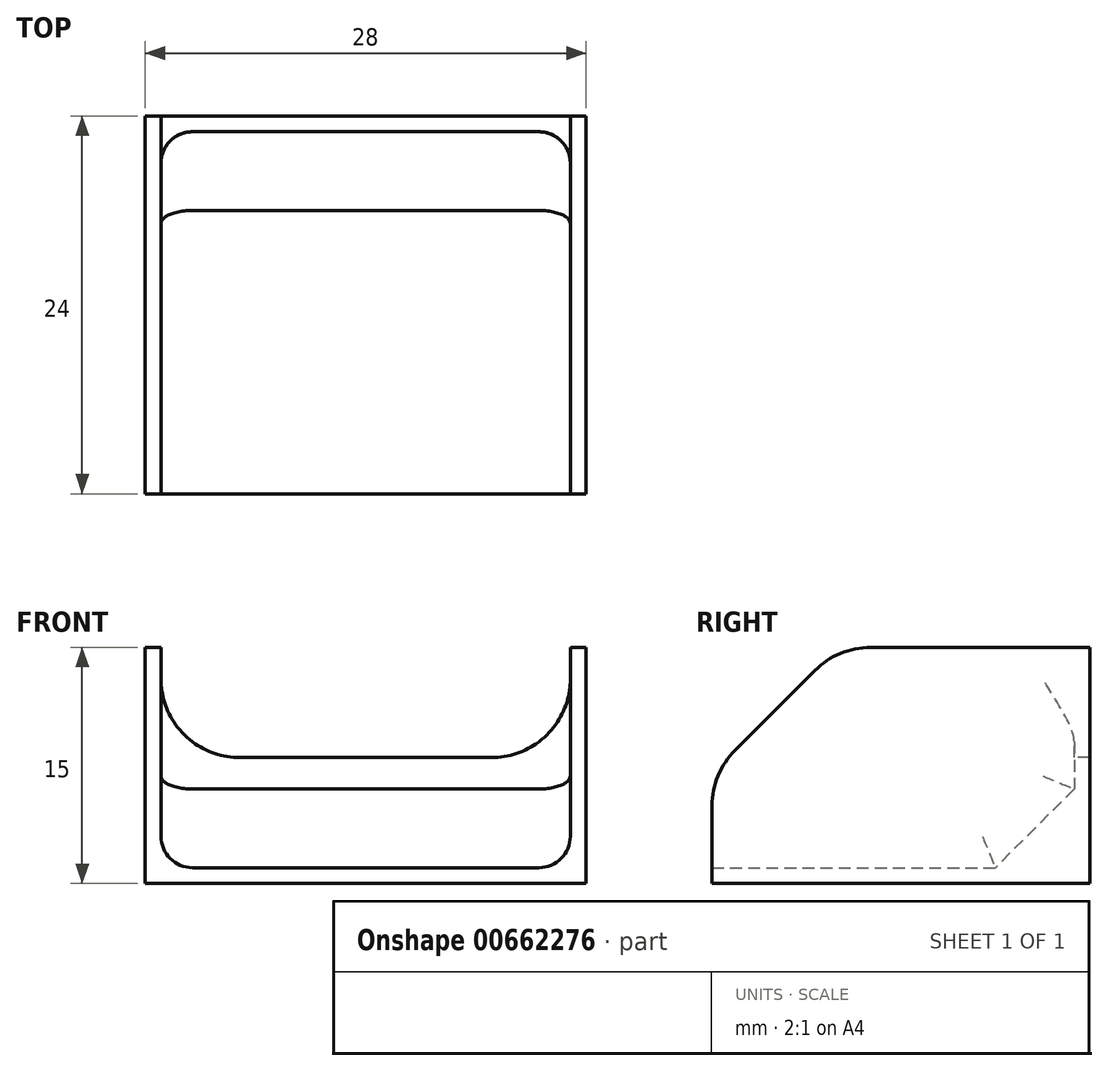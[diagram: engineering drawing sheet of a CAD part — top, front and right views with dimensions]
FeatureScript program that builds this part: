
annotation { "Feature Type Name" : "Feature", "Feature Type Description" : "" }
export const myFeature = defineFeature(function(context is Context, id is Id, definition is map)
    precondition{}
    {
        {
            var Q0;
            Q0=qCreatedBy(makeId("Top.planeOp"),FACE);
            var sketch = newSketch(context, id + "F0", { "sketchPlane" : qUnion([Q0])});
            skLineSegment(sketch, "E0.bottom", {"start": v(-34.7, 0) * mm, "end": v(-62.7, 0) * mm});
            skLineSegment(sketch, "E0.top", {"start": v(-34.7, 24) * mm, "end": v(-62.7, 24) * mm});
            skLineSegment(sketch, "E0.left", {"start": v(-34.7, 0) * mm, "end": v(-34.7, 24) * mm});
            skLineSegment(sketch, "E0.right", {"start": v(-62.7, 0) * mm, "end": v(-62.7, 24) * mm});
            skSolve(sketch);
        }
        {
            var Q0;
            Q0=makeQuery(id+"F0.imprint","IMPRINT",FACE,{"disambiguationData":[TD([[makeQuery(id+"F0.imprint","IMPRINT",EDGE,{"derivedFrom":sQuery(id+"F0.wireOp",EDGE,"E0.bottom")}),-1.0]])]});
            var sketch = newSketch(context, id + "F1", { "sketchPlane" : qUnion([Q0])});
            skSolve(sketch);
        }
        {
            var Q0;
            Q0=makeQuery(id+"F1.imprint","IMPRINT",FACE,{"disambiguationData":[TD([[makeQuery(id+"F1.imprint","IMPRINT",EDGE,{"derivedFrom":makeQuery(id+"F0.imprint","IMPRINT",EDGE,{"derivedFrom":sQuery(id+"F0.wireOp",EDGE,"E0.bottom")})}),-1.0]])]});
            extrude(context, id + "F2", {"entities" : qUnion([Q0]), "depth" : 15 * mm, "offsetDistance" : 25 * mm});
        }
        {
            var Q0;
            Q0=makeQuery(id+"F2.opExtrude","CAP_FACE",FACE,{"disambiguationData":[OSD([sQuery(id+"F0.wireOp",EDGE,"E0.bottom"),sQuery(id+"F0.wireOp",EDGE,"E0.top"),sQuery(id+"F0.wireOp",EDGE,"E0.left"),sQuery(id+"F0.wireOp",EDGE,"E0.right")])],"isStart":false});
            shell(context, id + "F3", {"entities" : qUnion([Q0]), "thickness" : 1 * mm});
        }
        {
            var Q0;
            Q0=makeQuery(id+"F3.opShell","OFFSET_FACE",FACE,{"disambiguationData":[OSD([sQuery(id+"F0.wireOp",EDGE,"E0.bottom")])]});
            extrude(context, id + "F4", {"entities" : qUnion([Q0]), "operationType" : NewBodyOperationType.REMOVE, "oppositeDirection" : true, "depth" : 25 * mm, "offsetDistance" : 25 * mm});
        }
        {
            var Q0;
            {var subQ0=sQuery(id+"F0.wireOp",EDGE,"E0.right");var subQ1=sQuery(id+"F0.wireOp",EDGE,"E0.bottom");Q0=makeQuery(id+"F4.boolean.opBoolean","SPLIT",EDGE,{"disambiguationData":[TD([makeQuery(id+"F2.opExtrude","SWEPT_FACE",FACE,{"disambiguationData":[OSD([subQ0])]})])],"derivedFrom":makeQuery(id+"F2.opExtrude","CAP_EDGE",EDGE,{"disambiguationData":[OSD([subQ1])],"isStart":false})});}
            var Q1;
            {var subQ0=sQuery(id+"F0.wireOp",EDGE,"E0.left");var subQ1=sQuery(id+"F0.wireOp",EDGE,"E0.bottom");Q1=makeQuery(id+"F4.boolean.opBoolean","SPLIT",EDGE,{"disambiguationData":[TD([makeQuery(id+"F2.opExtrude","SWEPT_FACE",FACE,{"disambiguationData":[OSD([subQ0])]})])],"derivedFrom":makeQuery(id+"F2.opExtrude","CAP_EDGE",EDGE,{"disambiguationData":[OSD([subQ1])],"isStart":false})});}
            chamfer(context, id + "F5", {"entities" : qUnion([Q0, Q1]), "width" : 8 * mm, "tangentPropagation" : true});
        }
        {
            var Q0;
            {var subQ0=sQuery(id+"F0.wireOp",EDGE,"E0.bottom");var subQ1=makeQuery(id+"F2.opExtrude","SWEPT_FACE",FACE,{"disambiguationData":[OSD([subQ0])]});var subQ2=sQuery(id+"F0.wireOp",EDGE,"E0.right");Q0=makeQuery(id+"F5.opChamfer","BLEND_EDGE",EDGE,{"blendedFrom":[makeQuery(id+"F4.boolean.opBoolean","SPLIT",EDGE,{"disambiguationData":[TD([makeQuery(id+"F2.opExtrude","SWEPT_FACE",FACE,{"disambiguationData":[OSD([subQ2])]})])],"derivedFrom":makeQuery(id+"F2.opExtrude","CAP_EDGE",EDGE,{"disambiguationData":[OSD([subQ0])],"isStart":false})}),subQ1],"blendedInto":[subQ1]});}
            var Q1;
            {var subQ0=sQuery(id+"F0.wireOp",EDGE,"E0.right");var subQ1=sQuery(id+"F0.wireOp",EDGE,"E0.bottom");var subQ2=makeQuery(id+"F2.opExtrude","CAP_FACE",FACE,{"disambiguationData":[OSD([subQ1,sQuery(id+"F0.wireOp",EDGE,"E0.top"),sQuery(id+"F0.wireOp",EDGE,"E0.left"),subQ0])],"isStart":false});Q1=makeQuery(id+"F5.opChamfer","BLEND_EDGE",EDGE,{"blendedFrom":[makeQuery(id+"F4.boolean.opBoolean","SPLIT",EDGE,{"disambiguationData":[TD([makeQuery(id+"F2.opExtrude","SWEPT_FACE",FACE,{"disambiguationData":[OSD([subQ0])]})])],"derivedFrom":makeQuery(id+"F2.opExtrude","CAP_EDGE",EDGE,{"disambiguationData":[OSD([subQ1])],"isStart":false})}),subQ2],"blendedInto":[subQ2]});}
            var Q2;
            {var subQ0=sQuery(id+"F0.wireOp",EDGE,"E0.left");var subQ1=sQuery(id+"F0.wireOp",EDGE,"E0.bottom");var subQ2=makeQuery(id+"F2.opExtrude","CAP_FACE",FACE,{"disambiguationData":[OSD([subQ1,sQuery(id+"F0.wireOp",EDGE,"E0.top"),subQ0,sQuery(id+"F0.wireOp",EDGE,"E0.right")])],"isStart":false});Q2=makeQuery(id+"F5.opChamfer","BLEND_EDGE",EDGE,{"blendedFrom":[makeQuery(id+"F4.boolean.opBoolean","SPLIT",EDGE,{"disambiguationData":[TD([makeQuery(id+"F2.opExtrude","SWEPT_FACE",FACE,{"disambiguationData":[OSD([subQ0])]})])],"derivedFrom":makeQuery(id+"F2.opExtrude","CAP_EDGE",EDGE,{"disambiguationData":[OSD([subQ1])],"isStart":false})}),subQ2],"blendedInto":[subQ2]});}
            var Q3;
            {var subQ0=sQuery(id+"F0.wireOp",EDGE,"E0.bottom");var subQ1=makeQuery(id+"F2.opExtrude","SWEPT_FACE",FACE,{"disambiguationData":[OSD([subQ0])]});var subQ2=sQuery(id+"F0.wireOp",EDGE,"E0.left");Q3=makeQuery(id+"F5.opChamfer","BLEND_EDGE",EDGE,{"blendedFrom":[makeQuery(id+"F4.boolean.opBoolean","SPLIT",EDGE,{"disambiguationData":[TD([makeQuery(id+"F2.opExtrude","SWEPT_FACE",FACE,{"disambiguationData":[OSD([subQ2])]})])],"derivedFrom":makeQuery(id+"F2.opExtrude","CAP_EDGE",EDGE,{"disambiguationData":[OSD([subQ0])],"isStart":false})}),subQ1],"blendedInto":[subQ1]});}
            fillet(context, id + "F6", {"entities" : qUnion([Q0, Q1, Q2, Q3]), "radius" : 5 * mm, "tangentPropagation" : true, "allowEdgeOverflow" : false});
        }
        {
            var Q0;
            Q0=makeQuery(id+"F3.opShell","OFFSET_FACE",FACE,{"disambiguationData":[OSD([sQuery(id+"F0.wireOp",EDGE,"E0.top")])]});
            var sketch = newSketch(context, id + "F7", { "sketchPlane" : qUnion([Q0])});
            skLineSegment(sketch, "E1.bottom", {"start": v(-61.7, 15) * mm, "end": v(-35.7, 15) * mm});
            skLineSegment(sketch, "E1.top", {"start": v(-61.7, 8) * mm, "end": v(-35.7, 8) * mm});
            skLineSegment(sketch, "E1.left", {"start": v(-61.7, 15) * mm, "end": v(-61.7, 8) * mm});
            skLineSegment(sketch, "E1.right", {"start": v(-35.7, 15) * mm, "end": v(-35.7, 8) * mm});
            skSolve(sketch);
        }
        {
            var Q0;
            Q0 = qSketchRegion(id + "F7", true);
            extrude(context, id + "F8", {"entities" : qUnion([Q0]), "operationType" : NewBodyOperationType.REMOVE, "oppositeDirection" : true, "depth" : 25 * mm, "offsetDistance" : 25 * mm});
        }
        {
            var Q0;
            Q0=makeQuery(id+"F8.boolean.opBoolean","COPY",EDGE,{"derivedFrom":makeQuery(id+"F8.opExtrude","SWEPT_EDGE",EDGE,{"disambiguationData":[OSD([sQuery(id+"F0.wireOp",EDGE,"E0.top"),sQuery(id+"F0.wireOp",EDGE,"E0.right"),sQuery(id+"F7.wireOp",EDGE,"E1.top"),sQuery(id+"F7.wireOp",EDGE,"E1.left")])]})});
            var Q1;
            Q1=makeQuery(id+"F8.boolean.opBoolean","COPY",EDGE,{"derivedFrom":makeQuery(id+"F8.opExtrude","SWEPT_EDGE",EDGE,{"disambiguationData":[OSD([sQuery(id+"F0.wireOp",EDGE,"E0.top"),sQuery(id+"F0.wireOp",EDGE,"E0.left"),sQuery(id+"F7.wireOp",EDGE,"E1.top"),sQuery(id+"F7.wireOp",EDGE,"E1.right")])]})});
            fillet(context, id + "F9", {"entities" : qUnion([Q0, Q1]), "radius" : 5 * mm, "tangentPropagation" : true, "allowEdgeOverflow" : false});
        }
        {
            var Q0;
            {var subQ0=sQuery(id+"F0.wireOp",EDGE,"E0.top");Q0=makeQuery(id+"F3.opShell","OFFSET_EDGE",EDGE,{"disambiguationData":[OSD([subQ0]),TDD([makeQuery(id+"F2.opExtrude","CAP_EDGE",EDGE,{"disambiguationData":[OSD([subQ0])],"isStart":true})])]});}
            chamfer(context, id + "F10", {"entities" : qUnion([Q0]), "width" : 5 * mm, "tangentPropagation" : true});
        }
        {
            var Q0;
            {var subQ0=sQuery(id+"F0.wireOp",EDGE,"E0.right");var subQ1=sQuery(id+"F0.wireOp",EDGE,"E0.bottom");Q0=makeQuery(id+"F4.boolean.opBoolean","MERGE",EDGE,{"derivedFrom":[makeQuery(id+"F3.opShell","OFFSET_EDGE",EDGE,{"disambiguationData":[OSD([subQ0]),TDD([makeQuery(id+"F2.opExtrude","CAP_EDGE",EDGE,{"disambiguationData":[OSD([subQ0])],"isStart":true})])]}),makeQuery(id+"F4.opExtrude","SWEPT_EDGE",EDGE,{"disambiguationData":[OSD([subQ1,subQ0]),TDD([makeQuery(id+"F3.opShell","OFFSET_VERTEX",VERTEX,{"disambiguationData":[OSD([subQ1,subQ0]),TDD([makeQuery(id+"F2.opExtrude","CAP_VERTEX",VERTEX,{"disambiguationData":[OSD([subQ1,subQ0])],"isStart":true})])]})])]})]});}
            var Q1;
            Q1=makeQuery(id+"F3.opShell","OFFSET_EDGE",EDGE,{"disambiguationData":[OSD([sQuery(id+"F0.wireOp",EDGE,"E0.top"),sQuery(id+"F0.wireOp",EDGE,"E0.right")])]});
            var Q2;
            {var subQ0=sQuery(id+"F0.wireOp",EDGE,"E0.right");var subQ1=sQuery(id+"F0.wireOp",EDGE,"E0.top");Q2=makeQuery(id+"F10.opChamfer","BLEND_EDGE",EDGE,{"blendedFrom":[makeQuery(id+"F3.opShell","OFFSET_EDGE",EDGE,{"disambiguationData":[OSD([subQ1]),TDD([makeQuery(id+"F2.opExtrude","CAP_EDGE",EDGE,{"disambiguationData":[OSD([subQ1])],"isStart":true})])]}),makeQuery(id+"F8.boolean.opBoolean","MERGE",FACE,{"derivedFrom":[makeQuery(id+"F4.boolean.opBoolean","MERGE",FACE,{"derivedFrom":[makeQuery(id+"F3.opShell","OFFSET_FACE",FACE,{"disambiguationData":[OSD([subQ0])]}),makeQuery(id+"F4.opExtrude","SWEPT_FACE",FACE,{"disambiguationData":[OSD([sQuery(id+"F0.wireOp",EDGE,"E0.bottom"),subQ0])]})]}),makeQuery(id+"F8.opExtrude","SWEPT_FACE",FACE,{"disambiguationData":[OSD([sQuery(id+"F7.wireOp",EDGE,"E1.left")])]})]})],"blendedInto":[makeQuery(id+"F8.boolean.opBoolean","MERGE",FACE,{"derivedFrom":[makeQuery(id+"F4.boolean.opBoolean","MERGE",FACE,{"derivedFrom":[makeQuery(id+"F3.opShell","OFFSET_FACE",FACE,{"disambiguationData":[OSD([subQ0])]}),makeQuery(id+"F4.opExtrude","SWEPT_FACE",FACE,{"disambiguationData":[OSD([sQuery(id+"F0.wireOp",EDGE,"E0.bottom"),subQ0])]})]}),makeQuery(id+"F8.opExtrude","SWEPT_FACE",FACE,{"disambiguationData":[OSD([sQuery(id+"F7.wireOp",EDGE,"E1.left")])]})]})]});}
            var Q3;
            {var subQ0=sQuery(id+"F0.wireOp",EDGE,"E0.left");var subQ1=sQuery(id+"F0.wireOp",EDGE,"E0.bottom");Q3=makeQuery(id+"F4.boolean.opBoolean","MERGE",EDGE,{"derivedFrom":[makeQuery(id+"F3.opShell","OFFSET_EDGE",EDGE,{"disambiguationData":[OSD([subQ0]),TDD([makeQuery(id+"F2.opExtrude","CAP_EDGE",EDGE,{"disambiguationData":[OSD([subQ0])],"isStart":true})])]}),makeQuery(id+"F4.opExtrude","SWEPT_EDGE",EDGE,{"disambiguationData":[OSD([subQ1,subQ0]),TDD([makeQuery(id+"F3.opShell","OFFSET_VERTEX",VERTEX,{"disambiguationData":[OSD([subQ1,subQ0]),TDD([makeQuery(id+"F2.opExtrude","CAP_VERTEX",VERTEX,{"disambiguationData":[OSD([subQ1,subQ0])],"isStart":true})])]})])]})]});}
            var Q4;
            {var subQ0=sQuery(id+"F0.wireOp",EDGE,"E0.left");var subQ1=sQuery(id+"F0.wireOp",EDGE,"E0.top");Q4=makeQuery(id+"F10.opChamfer","BLEND_EDGE",EDGE,{"blendedFrom":[makeQuery(id+"F3.opShell","OFFSET_EDGE",EDGE,{"disambiguationData":[OSD([subQ1]),TDD([makeQuery(id+"F2.opExtrude","CAP_EDGE",EDGE,{"disambiguationData":[OSD([subQ1])],"isStart":true})])]}),makeQuery(id+"F8.boolean.opBoolean","MERGE",FACE,{"derivedFrom":[makeQuery(id+"F4.boolean.opBoolean","MERGE",FACE,{"derivedFrom":[makeQuery(id+"F3.opShell","OFFSET_FACE",FACE,{"disambiguationData":[OSD([subQ0])]}),makeQuery(id+"F4.opExtrude","SWEPT_FACE",FACE,{"disambiguationData":[OSD([sQuery(id+"F0.wireOp",EDGE,"E0.bottom"),subQ0])]})]}),makeQuery(id+"F8.opExtrude","SWEPT_FACE",FACE,{"disambiguationData":[OSD([sQuery(id+"F7.wireOp",EDGE,"E1.right")])]})]})],"blendedInto":[makeQuery(id+"F8.boolean.opBoolean","MERGE",FACE,{"derivedFrom":[makeQuery(id+"F4.boolean.opBoolean","MERGE",FACE,{"derivedFrom":[makeQuery(id+"F3.opShell","OFFSET_FACE",FACE,{"disambiguationData":[OSD([subQ0])]}),makeQuery(id+"F4.opExtrude","SWEPT_FACE",FACE,{"disambiguationData":[OSD([sQuery(id+"F0.wireOp",EDGE,"E0.bottom"),subQ0])]})]}),makeQuery(id+"F8.opExtrude","SWEPT_FACE",FACE,{"disambiguationData":[OSD([sQuery(id+"F7.wireOp",EDGE,"E1.right")])]})]})]});}
            var Q5;
            Q5=makeQuery(id+"F3.opShell","OFFSET_EDGE",EDGE,{"disambiguationData":[OSD([sQuery(id+"F0.wireOp",EDGE,"E0.top"),sQuery(id+"F0.wireOp",EDGE,"E0.left")])]});
            fillet(context, id + "F11", {"entities" : qUnion([Q0, Q1, Q2, Q3, Q4, Q5]), "radius" : 2 * mm, "tangentPropagation" : true, "allowEdgeOverflow" : false});
        }
    });
